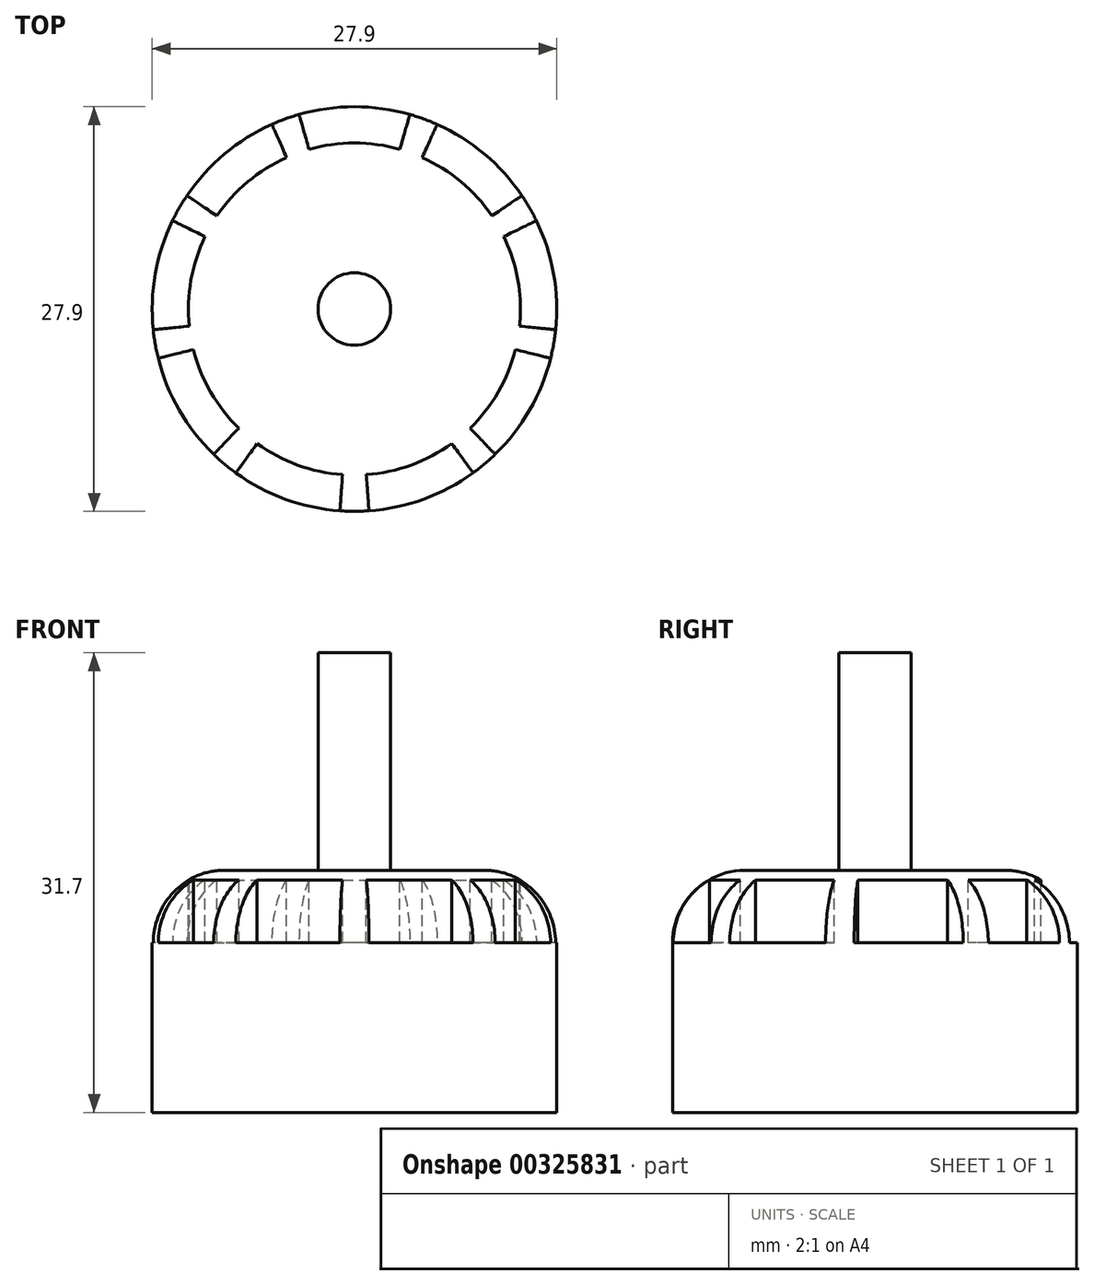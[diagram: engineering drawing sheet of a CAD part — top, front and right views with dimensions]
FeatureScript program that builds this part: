
annotation { "Feature Type Name" : "Feature", "Feature Type Description" : "" }
export const myFeature = defineFeature(function(context is Context, id is Id, definition is map)
    precondition{}
    {
        {
            var Q0;
            Q0=qCreatedBy(makeId("Top.planeOp"),FACE);
            var sketch = newSketch(context, id + "F0", { "sketchPlane" : qUnion([Q0])});
            skCircle(sketch, "E0", {"center": v(0, 0) * mm, "radius": 13.95 * mm});
            skSolve(sketch);
        }
        {
            var Q0;
            Q0=qSketchRegion(id+"F0",true);
            extrude(context, id + "F1", {"entities" : qUnion([Q0]), "depth" : (31.7 - 15) * mm});
        }
        {
            var Q0;
            Q0=makeQuery(id+"F1.opExtrude","CAP_EDGE",EDGE,{"disambiguationData":[OSD([sQuery(id+"F0.wireOp",EDGE,"E0")])],"isStart":false});
            fillet(context, id + "F2", {"entities" : qUnion([Q0]), "radius" : 5 * mm, "tangentPropagation" : true, "allowEdgeOverflow" : false});
        }
        {
            var Q0;
            Q0=makeQuery(id+"F1.opExtrude","CAP_FACE",FACE,{"disambiguationData":[OSD([sQuery(id+"F0.wireOp",EDGE,"E0")])],"isStart":false});
            var sketch = newSketch(context, id + "F3", { "sketchPlane" : qUnion([Q0])});
            skArc(sketch, "E1", {"start": v(-3.13, 11.01) * mm, "mid": v(-1.58, 11.34) * mm, "end": v(0, 11.45) * mm});
            skLineSegment(sketch, "E2", {"start": v(0, 0) * mm, "end": v(0, 11.45) * mm, "construction": true});
            skArc(sketch, "E3", {"start": v(-3.82, 13.42) * mm, "mid": v(-1.93, 13.82) * mm, "end": v(0, 13.95) * mm});
            skLineSegment(sketch, "E4", {"start": v(-3.82, 13.42) * mm, "end": v(-3.13, 11.01) * mm});
            skArc(sketch, "E5.MirrorCS", {"start": v(3.82, 13.42) * mm, "mid": v(1.93, 13.82) * mm, "end": v(0, 13.95) * mm});
            skLineSegment(sketch, "E6.MirrorCS", {"start": v(3.82, 13.42) * mm, "end": v(3.13, 11.01) * mm});
            skArc(sketch, "E7.MirrorCS", {"start": v(3.13, 11.01) * mm, "mid": v(1.58, 11.34) * mm, "end": v(0, 11.45) * mm});
            skLineSegment(sketch, "E8.1.0", {"start": v(-11.55, 7.82) * mm, "end": v(-9.48, 6.42) * mm});
            skArc(sketch, "E8.1.1", {"start": v(-9.48, 6.42) * mm, "mid": v(-8.5, 7.67) * mm, "end": v(-7.36, 8.77) * mm});
            skArc(sketch, "E8.1.2", {"start": v(-4.68, 10.45) * mm, "mid": v(-6.08, 9.7) * mm, "end": v(-7.36, 8.77) * mm});
            skLineSegment(sketch, "E8.1.3", {"start": v(-5.7, 12.73) * mm, "end": v(-4.68, 10.45) * mm});
            skArc(sketch, "E8.1.4", {"start": v(-5.7, 12.73) * mm, "mid": v(-7.4, 11.82) * mm, "end": v(-8.97, 10.69) * mm});
            skArc(sketch, "E8.1.5", {"start": v(-11.55, 7.82) * mm, "mid": v(-10.36, 9.34) * mm, "end": v(-8.97, 10.69) * mm});
            skLineSegment(sketch, "E8.2.0", {"start": v(-13.88, -1.43) * mm, "end": v(-11.39, -1.17) * mm});
            skArc(sketch, "E8.2.1", {"start": v(-11.39, -1.17) * mm, "mid": v(-11.44, 0.41) * mm, "end": v(-11.28, 1.99) * mm});
            skArc(sketch, "E8.2.2", {"start": v(-10.3, 5) * mm, "mid": v(-10.9, 3.53) * mm, "end": v(-11.28, 1.99) * mm});
            skLineSegment(sketch, "E8.2.3", {"start": v(-12.55, 6.1) * mm, "end": v(-10.3, 5) * mm});
            skArc(sketch, "E8.2.4", {"start": v(-12.55, 6.1) * mm, "mid": v(-13.27, 4.3) * mm, "end": v(-13.74, 2.42) * mm});
            skArc(sketch, "E8.2.5", {"start": v(-13.88, -1.43) * mm, "mid": v(-13.94, 0.5) * mm, "end": v(-13.74, 2.42) * mm});
            skLineSegment(sketch, "E9.2.3.0", {"start": v(-9.7, -10.02) * mm, "end": v(-7.97, -8.22) * mm});
            skArc(sketch, "E9.3.3.0", {"start": v(-7.97, -8.22) * mm, "mid": v(-9.03, -7.04) * mm, "end": v(-9.92, -5.72) * mm});
            skArc(sketch, "E9.7.3.0", {"start": v(-11.1, -2.8) * mm, "mid": v(-10.61, -4.3) * mm, "end": v(-9.92, -5.72) * mm});
            skLineSegment(sketch, "E9.11.3.0", {"start": v(-13.53, -3.4) * mm, "end": v(-11.1, -2.8) * mm});
            skArc(sketch, "E9.14.3.0", {"start": v(-13.53, -3.4) * mm, "mid": v(-12.93, -5.24) * mm, "end": v(-12.08, -6.97) * mm});
            skArc(sketch, "E9.18.3.0", {"start": v(-9.7, -10.02) * mm, "mid": v(-11, -8.58) * mm, "end": v(-12.08, -6.97) * mm});
            skLineSegment(sketch, "E9.2.4.0", {"start": v(-1, -13.91) * mm, "end": v(-0.82, -11.42) * mm});
            skArc(sketch, "E9.3.4.0", {"start": v(-0.82, -11.42) * mm, "mid": v(-2.4, -11.2) * mm, "end": v(-3.92, -10.76) * mm});
            skArc(sketch, "E9.7.4.0", {"start": v(-6.71, -9.28) * mm, "mid": v(-5.37, -10.11) * mm, "end": v(-3.92, -10.76) * mm});
            skLineSegment(sketch, "E9.11.4.0", {"start": v(-8.18, -11.3) * mm, "end": v(-6.71, -9.28) * mm});
            skArc(sketch, "E9.14.4.0", {"start": v(-8.18, -11.3) * mm, "mid": v(-6.54, -12.32) * mm, "end": v(-4.77, -13.1) * mm});
            skArc(sketch, "E9.18.4.0", {"start": v(-1, -13.91) * mm, "mid": v(-2.91, -13.64) * mm, "end": v(-4.77, -13.1) * mm});
            skLineSegment(sketch, "E9.2.5.0", {"start": v(8.18, -11.3) * mm, "end": v(6.71, -9.28) * mm});
            skArc(sketch, "E9.3.5.0", {"start": v(6.71, -9.28) * mm, "mid": v(5.37, -10.11) * mm, "end": v(3.92, -10.76) * mm});
            skArc(sketch, "E9.7.5.0", {"start": v(0.82, -11.42) * mm, "mid": v(2.4, -11.2) * mm, "end": v(3.92, -10.76) * mm});
            skLineSegment(sketch, "E9.11.5.0", {"start": v(1, -13.91) * mm, "end": v(0.82, -11.42) * mm});
            skArc(sketch, "E9.14.5.0", {"start": v(1, -13.91) * mm, "mid": v(2.91, -13.64) * mm, "end": v(4.77, -13.1) * mm});
            skArc(sketch, "E9.18.5.0", {"start": v(8.18, -11.3) * mm, "mid": v(6.54, -12.32) * mm, "end": v(4.77, -13.1) * mm});
            skLineSegment(sketch, "E9.2.6.0", {"start": v(13.53, -3.4) * mm, "end": v(11.1, -2.8) * mm});
            skArc(sketch, "E9.3.6.0", {"start": v(11.1, -2.8) * mm, "mid": v(10.61, -4.3) * mm, "end": v(9.92, -5.73) * mm});
            skArc(sketch, "E9.7.6.0", {"start": v(7.97, -8.22) * mm, "mid": v(9.03, -7.04) * mm, "end": v(9.92, -5.73) * mm});
            skLineSegment(sketch, "E9.11.6.0", {"start": v(9.7, -10.02) * mm, "end": v(7.97, -8.22) * mm});
            skArc(sketch, "E9.14.6.0", {"start": v(9.7, -10.02) * mm, "mid": v(11, -8.58) * mm, "end": v(12.08, -6.98) * mm});
            skArc(sketch, "E9.18.6.0", {"start": v(13.53, -3.4) * mm, "mid": v(12.93, -5.24) * mm, "end": v(12.08, -6.98) * mm});
            skLineSegment(sketch, "E9.2.7.0", {"start": v(12.55, 6.1) * mm, "end": v(10.3, 5) * mm});
            skArc(sketch, "E9.3.7.0", {"start": v(10.3, 5) * mm, "mid": v(10.9, 3.53) * mm, "end": v(11.28, 1.99) * mm});
            skArc(sketch, "E9.7.7.0", {"start": v(11.39, -1.17) * mm, "mid": v(11.44, 0.41) * mm, "end": v(11.28, 1.99) * mm});
            skLineSegment(sketch, "E9.11.7.0", {"start": v(13.88, -1.43) * mm, "end": v(11.39, -1.17) * mm});
            skArc(sketch, "E9.14.7.0", {"start": v(13.88, -1.43) * mm, "mid": v(13.94, 0.5) * mm, "end": v(13.74, 2.42) * mm});
            skArc(sketch, "E9.18.7.0", {"start": v(12.55, 6.1) * mm, "mid": v(13.27, 4.3) * mm, "end": v(13.74, 2.42) * mm});
            skLineSegment(sketch, "E10.2.8.0", {"start": v(5.7, 12.73) * mm, "end": v(4.68, 10.45) * mm});
            skArc(sketch, "E10.3.8.0", {"start": v(4.68, 10.45) * mm, "mid": v(6.08, 9.7) * mm, "end": v(7.36, 8.77) * mm});
            skArc(sketch, "E10.7.8.0", {"start": v(9.48, 6.42) * mm, "mid": v(8.5, 7.67) * mm, "end": v(7.36, 8.77) * mm});
            skLineSegment(sketch, "E10.11.8.0", {"start": v(11.55, 7.82) * mm, "end": v(9.48, 6.42) * mm});
            skArc(sketch, "E10.14.8.0", {"start": v(11.55, 7.82) * mm, "mid": v(10.36, 9.34) * mm, "end": v(8.97, 10.69) * mm});
            skArc(sketch, "E10.18.8.0", {"start": v(5.7, 12.73) * mm, "mid": v(7.4, 11.82) * mm, "end": v(8.97, 10.69) * mm});
            skSolve(sketch);
        }
        {
            var Q0;
            Q0=qSketchRegion(id+"F3",true);
            extrude(context, id + "F4", {"entities" : qUnion([Q0]), "operationType" : NewBodyOperationType.REMOVE, "oppositeDirection" : true, "depth" : 5 * mm});
        }
        {
            var Q0;
            Q0=makeQuery(id+"F1.opExtrude","CAP_FACE",FACE,{"disambiguationData":[OSD([sQuery(id+"F0.wireOp",EDGE,"E0")])],"isStart":false});
            var sketch = newSketch(context, id + "F5", { "sketchPlane" : qUnion([Q0])});
            skCircle(sketch, "E11", {"center": v(0, 0) * mm, "radius": 2.5 * mm});
            skSolve(sketch);
        }
        {
            var Q0;
            Q0=qSketchRegion(id+"F5",true);
            extrude(context, id + "F6", {"entities" : qUnion([Q0]), "operationType" : NewBodyOperationType.ADD, "depth" : 15 * mm});
        }
    });
